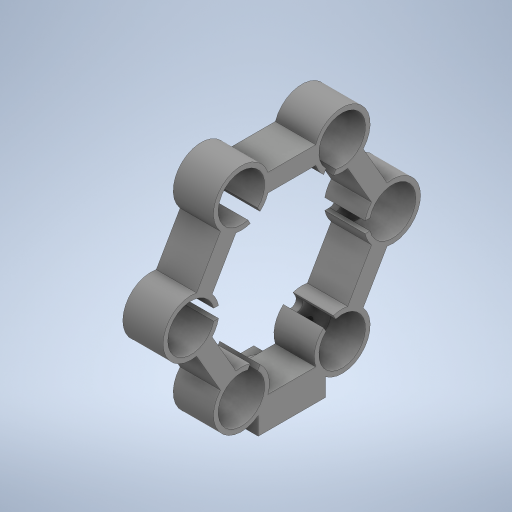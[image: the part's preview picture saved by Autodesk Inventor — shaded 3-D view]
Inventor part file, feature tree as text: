
AUTODESK INVENTOR PART (.ipt)
format: ipt  version: 2023 (Build 270158000, 158)  size: 482,816 bytes
history: native  units: in
note: dims shown in document units (in); Inventor stores cm internally (conversion verified against a paired STEP export)
features: extrude x6, sketch x3, projected_geometry x1
ambient origin geometry x8: Origin, YZ Plane, XZ Plane, XY Plane, X Axis, Y Axis, Z Axis, Center Point
bodies: Solid1 (feature_tree)
feature tree (10):
  sketch  "Sketch1"  dims[d0=1.378in d1=1.7717in]
  extrude  "Extrusion1"  Depth=1.7717in
  extrude  "Extrusion2"  Depth=0.8189in
  extrude  "Extrusion3"  Depth=0.315in
  extrude  "Extrusion4"  Depth=0.315in
  extrude  "Extrusion5"  Depth=0.1969in TaperAngle=360.0deg
  extrude  "Extrusion6"  Depth=0.1575in
  sketch  "Sketch2"  dims[d2=0.9843in d3=0.8189in]
  sketch  "Sketch3"  dims[d4=1.1811in d5=0.315in d6=0.315in d7=2.3622in d9=360.0deg d11=0.1575in d12=0.1575in d13=2.3622in d15=360.0deg d17=0.0984in d18=0.0984in d20=2.3622in d22=360.0deg d24=1.1811in d25=0.315in d26=1.1811in d28=1.378in d29=1.378in d30=0.1575in d31=0.7087in d32=0.0in d33=0.5906in d34=0.0in d35=0.1575in d36=2.3622in d38=360.0deg d40=0.7087in d41=0.0in d42=1.2598in d43=0.0in d44=0.1181in d45=0.1969in d46=0.0in d47=0.7874in d48=0.7874in d49=0.1181in d50=1.5748in d52=360.0deg d54=0.1969in d55=0.0in d56=0.0197in d57=0.0344in]
  projected_geometry  "Projected Loop1"
